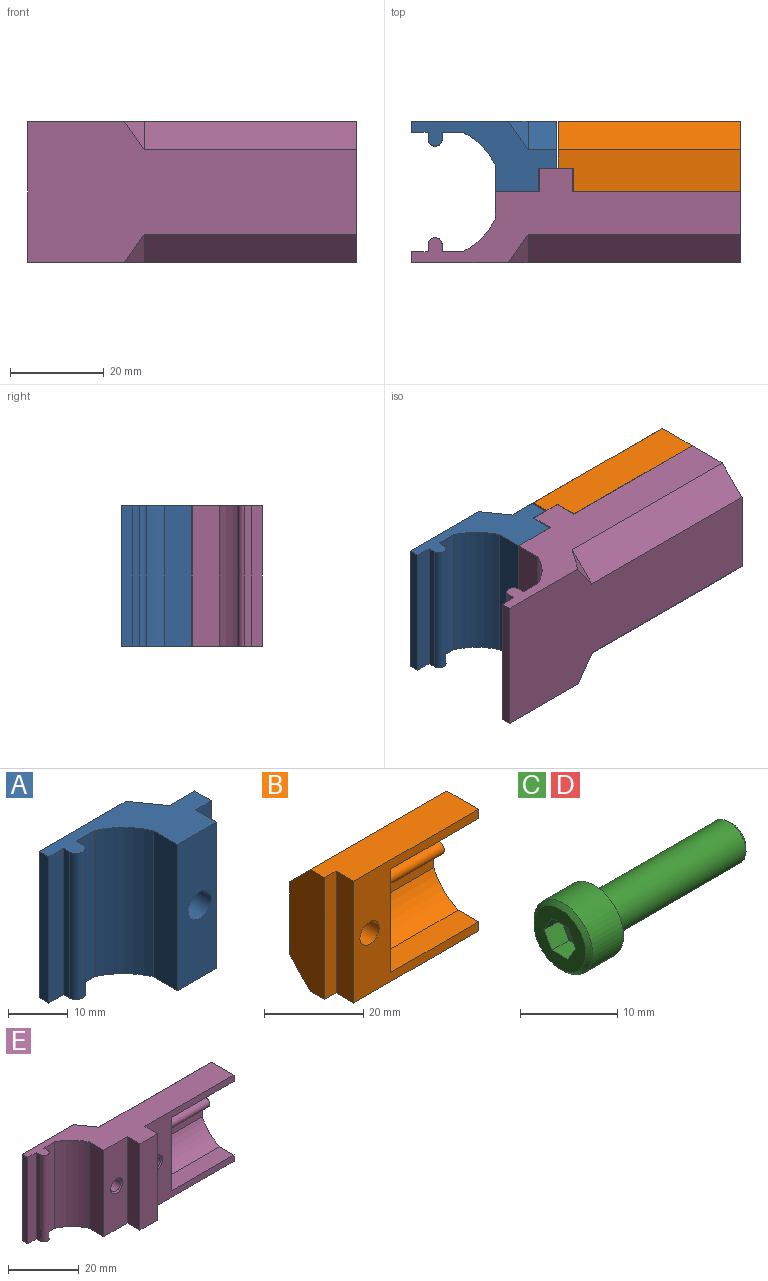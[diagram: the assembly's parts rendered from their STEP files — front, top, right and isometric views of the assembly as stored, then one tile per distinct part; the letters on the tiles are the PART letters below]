
ASSEMBLY  parts=5 mates=4
PART A: 23 faces, bbox 30.8x15x30 mm
  f0: plane 9.5x9.5mm, normal (0,1,0), area 41.7mm2, adj f1,f4
  f1: cone r=0mm half-angle=45deg, axis (0,1,0), area 7.7mm2, adj f0,f5
  f2: plane 6x6mm, normal (0,0.71,-0.71), area 50.9mm2, adj f3,f6,f8,f11
  f3: plane 6x6mm, normal (0.71,0.5,-0.5), area 25.5mm2, adj f2,f6,f11
  f4: cylinder r=4.75mm len=9.5mm, axis (0,-1,0), area 161.2mm2, adj f0,f11
  f5: cylinder r=2.75mm len=9.3mm, axis (0,-1,0), area 160.7mm2, adj f1,f20
  f6: plane 30.8x15mm, normal (0,0,-1), area 194.6mm2, adj f2,f3,f7,f8,f11,f12,f13,f14
  f7: plane 30x3.75mm, normal (0,-1,0), area 112.5mm2, adj f6,f8,f21,f22
  f8: plane 30x10mm, normal (1,0,0), area 264mm2, adj f2,f6,f7,f9,f11,f22
  f9: plane 6x6mm, normal (0,0.71,0.71), area 50.9mm2, adj f8,f10,f11,f22
  f10: plane 6x6mm, normal (0.71,0.5,0.5), area 25.5mm2, adj f9,f11,f22
  f11: plane 30.8x30mm, normal (0,1,0), area 755.7mm2, adj f2,f3,f4,f6,f8,f9,f10,f12
  f12: plane 30x2.25mm, normal (-1,0,0), area 67.5mm2, adj f6,f11,f13,f22
  f13: plane 30x3.5mm, normal (0,-1,0), area 105mm2, adj f6,f12,f14,f22
  f14: plane 30x1.5mm, normal (-1,0,0), area 45mm2, adj f6,f13,f15,f22
  f15: cylinder r=1.5mm len=30mm, axis (0,0,-1), area 141.4mm2, adj f6,f14,f16,f22
  f16: plane 30x1.5mm, normal (1,0,0), area 45mm2, adj f6,f15,f17,f22
  f17: plane 30x4.28mm, normal (0,-1,0), area 128.5mm2, adj f6,f16,f18,f22
  f18: cylinder r=14mm len=30mm, axis (0,0,-1), area 302.1mm2, adj f6,f17,f19,f22
  f19: plane 30x5.78mm, normal (-1,0,0), area 173.5mm2, adj f6,f18,f20,f22
  f20: plane 30x9.3mm, normal (0,-1,0), area 255.2mm2, adj f5,f6,f19,f21,f22
  f21: plane 30x5mm, normal (1,0,0), area 150mm2, adj f6,f7,f20,f22
  f22: plane 30.8x15mm, normal (0,0,1), area 194.6mm2, adj f7,f8,f9,f10,f11,f12,f13,f14
PART B: 24 faces, bbox 38.8x15x30 mm
  f0: plane 9.5x9.5mm, normal (0,1,0), area 41.7mm2, adj f1,f2
  f1: cone r=0mm half-angle=45deg, axis (0,1,0), area 7.7mm2, adj f0,f4
  f2: cylinder r=4.75mm len=9.5mm, axis (0,-1,0), area 161.2mm2, adj f0,f15
  f3: plane 25.5x12.75mm, normal (1,0,0), area 280.4mm2, adj f5,f6,f7,f8,f9,f10,f11,f12
  f4: cylinder r=2.75mm len=9.3mm, axis (0,-1,0), area 160.7mm2, adj f1,f19
  f5: plane 25x5.78mm, normal (0,0,-1), area 144.6mm2, adj f3,f6,f19,f20
  f6: cylinder r=14mm len=25mm, axis (1,0,0), area 251.7mm2, adj f3,f5,f7,f20
  f7: plane 25x4.28mm, normal (0,-1,0), area 107.1mm2, adj f3,f6,f8,f20
  f8: plane 25x1.5mm, normal (0,0,1), area 37.5mm2, adj f3,f7,f9,f20
  f9: cylinder r=1.5mm len=25mm, axis (1,0,0), area 117.8mm2, adj f3,f8,f10,f20
  f10: plane 25x1.5mm, normal (0,0,-1), area 37.5mm2, adj f3,f9,f11,f20
  f11: plane 25x4.28mm, normal (0,-1,0), area 107.1mm2, adj f3,f10,f12,f20
  f12: cylinder r=14mm len=25mm, axis (1,0,0), area 251.7mm2, adj f3,f11,f13,f20
  f13: plane 25x5.78mm, normal (0,0,1), area 144.6mm2, adj f3,f12,f19,f20
  f14: plane 38.8x9mm, normal (0,0,-1), area 332.9mm2, adj f16,f17,f18,f19,f20,f22
  f15: plane 38.8x18mm, normal (0,1,0), area 627.5mm2, adj f2,f16,f20,f21,f22
  f16: plane 38.8x6mm, normal (0,0.71,-0.71), area 329.2mm2, adj f14,f15,f20,f22
  f17: plane 30x3.25mm, normal (0,-1,0), area 97.5mm2, adj f14,f18,f22,f23
  f18: plane 30x5mm, normal (-1,0,0), area 150mm2, adj f14,f17,f19,f23
  f19: plane 35.55x30mm, normal (0,-1,0), area 405.2mm2, adj f3,f4,f5,f13,f14,f18,f20,f23
  f20: plane 30x15mm, normal (1,0,0), area 133.6mm2, adj f5,f6,f7,f8,f9,f10,f11,f12
  f21: plane 38.8x6mm, normal (0,0.71,0.71), area 329.2mm2, adj f15,f20,f22,f23
  f22: plane 30x10mm, normal (-1,0,0), area 264mm2, adj f14,f15,f16,f17,f21,f23
  f23: plane 38.8x9mm, normal (0,0,1), area 333mm2, adj f17,f18,f19,f20,f21,f22
PART C: 20 faces, bbox 25x8.5x8.5 mm
  f0: plane 4.02x4.02mm, normal (1,0,0), area 12.7mm2, adj f1
  f1: cone r=0mm half-angle=45deg, axis (-1,0,0), area 9.8mm2, adj f0,f2
  f2: cylinder r=2.5mm len=19.51mm, axis (1,0,0), area 306.5mm2, adj f1,f3
  f3: plane 8.5x8.5mm, normal (1,0,0), area 37.1mm2, adj f2,f5
  f4: cone r=0mm half-angle=75deg, axis (-1,0,0), area 13mm2, adj f6,f7,f8,f9,f10,f11
  f5: cylinder r=4.25mm len=8.5mm, axis (1,0,0), area 120.2mm2, adj f3,f12
  f6: plane 1.73x1mm, normal (-1,0,0), area 0.2mm2, adj f4,f13,f14
  f7: plane 1.73x1mm, normal (-1,0,0), area 0.2mm2, adj f4,f14,f15
  f8: plane 2x0.58mm, normal (-1,0,0), area 0.2mm2, adj f4,f15,f16
  f9: plane 1.73x1mm, normal (-1,0,0), area 0.2mm2, adj f4,f16,f17
  f10: plane 1.73x1mm, normal (-1,0,0), area 0.2mm2, adj f4,f17,f18
  f11: plane 2x0.58mm, normal (-1,0,0), area 0.2mm2, adj f4,f13,f18
  f12: cone r=0mm half-angle=45deg, axis (1,0,0), area 17.8mm2, adj f5,f19
  f13: plane 2.5x2mm, normal (0,0.87,0.5), area 5.8mm2, adj f6,f11,f14,f18,f19
  f14: plane 2.5x2.31mm, normal (0,0,1), area 5.8mm2, adj f6,f7,f13,f15,f19
  f15: plane 2.5x2mm, normal (0,-0.87,0.5), area 5.8mm2, adj f7,f8,f14,f16,f19
  f16: plane 2.5x2mm, normal (0,-0.87,-0.5), area 5.8mm2, adj f8,f9,f15,f17,f19
  f17: plane 2.5x2.31mm, normal (0,0,-1), area 5.8mm2, adj f9,f10,f16,f18,f19
  f18: plane 2.5x2mm, normal (0,0.87,-0.5), area 5.8mm2, adj f10,f11,f13,f17,f19
  f19: plane 7.5x7.5mm, normal (-1,0,0), area 30.3mm2, adj f12,f13,f14,f15,f16,f17,f18
PART D: same geometry as C
PART E: 37 faces, bbox 70x20x30 mm
  f0: cone r=0mm half-angle=60deg, axis (0,-1,0), area 15.5mm2, adj f1
  f1: cylinder r=2.07mm len=10.17mm, axis (0,-1,0), area 132mm2, adj f0,f12
  f2: cylinder r=14mm len=25mm, axis (1,0,0), area 251.7mm2, adj f3,f10,f11,f17
  f3: plane 25x4.28mm, normal (0,-1,0), area 107.1mm2, adj f2,f4,f10,f17
  f4: plane 25x1.5mm, normal (0,0,1), area 37.5mm2, adj f3,f5,f10,f17
  f5: cylinder r=1.5mm len=25mm, axis (1,0,0), area 117.8mm2, adj f4,f6,f10,f17
  f6: plane 25x1.5mm, normal (0,0,-1), area 37.5mm2, adj f5,f7,f10,f17
  f7: plane 25x4.28mm, normal (0,-1,0), area 107.1mm2, adj f6,f8,f10,f17
  f8: cylinder r=14mm len=25mm, axis (1,0,0), area 251.7mm2, adj f7,f9,f10,f17
  f9: plane 25x5.78mm, normal (0,0,1), area 144.6mm2, adj f8,f10,f17,f18
  f10: plane 25.5x12.75mm, normal (1,0,0), area 280.4mm2, adj f2,f3,f4,f5,f6,f7,f8,f9
  f11: plane 25x5.78mm, normal (0,0,-1), area 144.6mm2, adj f2,f10,f17,f18
  f12: cone r=0mm half-angle=45deg, axis (0,-1,0), area 8.8mm2, adj f1,f18
  f13: cone r=0mm half-angle=60deg, axis (0,-1,0), area 15.5mm2, adj f30
  f14: plane 45.2x6mm, normal (0,0.71,0.71), area 383.5mm2, adj f15,f17,f28,f32
  f15: plane 6x6mm, normal (0.71,0.5,0.5), area 25.5mm2, adj f14,f28,f32
  f16: plane 45.2x6mm, normal (0,0.71,-0.71), area 383.5mm2, adj f17,f28,f29,f34
  f17: plane 30x15mm, normal (1,0,0), area 133.6mm2, adj f2,f3,f4,f5,f6,f7,f8,f9
  f18: plane 35.7x30mm, normal (0,-1,0), area 413.9mm2, adj f9,f10,f11,f12,f17,f19,f32,f34
  f19: plane 30x5mm, normal (1,0,0), area 150mm2, adj f18,f20,f32,f34
  f20: plane 30x7mm, normal (0,-1,0), area 210mm2, adj f19,f31,f32,f34
  f21: cylinder r=14mm len=30mm, axis (0,0,-1), area 302.1mm2, adj f22,f32,f33,f34
  f22: plane 30x4.28mm, normal (0,-1,0), area 128.5mm2, adj f21,f23,f32,f34
  f23: plane 30x1.5mm, normal (1,0,0), area 45mm2, adj f22,f24,f32,f34
  f24: cylinder r=1.5mm len=30mm, axis (0,0,-1), area 141.4mm2, adj f23,f25,f32,f34
  f25: plane 30x1.5mm, normal (-1,0,0), area 45mm2, adj f24,f26,f32,f34
  f26: plane 30x3.5mm, normal (0,-1,0), area 105mm2, adj f25,f27,f32,f34
  f27: plane 30x2.25mm, normal (-1,0,0), area 67.5mm2, adj f26,f28,f32,f34
  f28: plane 70x30mm, normal (0,1,0), area 1532.1mm2, adj f14,f15,f16,f17,f27,f29,f32,f34
  f29: plane 6x6mm, normal (0.71,0.5,-0.5), area 25.5mm2, adj f16,f28,f34
  f30: cylinder r=2.07mm len=10.17mm, axis (0,-1,0), area 132mm2, adj f13,f35
  f31: plane 30x5mm, normal (-1,0,0), area 150mm2, adj f20,f32,f34,f36
  f32: plane 70x20mm, normal (0,0,1), area 601.1mm2, adj f14,f15,f17,f18,f19,f20,f21,f22
  f33: plane 30x5.78mm, normal (-1,0,0), area 173.5mm2, adj f21,f32,f34,f36
  f34: plane 70x20mm, normal (0,0,-1), area 601.1mm2, adj f16,f17,f18,f19,f20,f21,f22,f23
  f35: cone r=0mm half-angle=45deg, axis (0,-1,0), area 8.8mm2, adj f30,f36
  f36: plane 30x9.55mm, normal (0,-1,0), area 266.9mm2, adj f31,f32,f33,f34,f35
PLACE A t=(-7.14,-22.58,-11.41)mm
PLACE B t=(24.06,-22.58,-11.41)mm
PLACE C rot(axis=(0.58,-0.58,-0.58),120deg) t=(15.86,-12.98,-11.41)mm
PLACE D rot(axis=(0.58,-0.58,-0.58),120deg) t=(31.86,-12.98,-11.41)mm
PLACE E rot(axis=(1,0,0),180deg) t=(-7.14,-22.58,-11.41)mm
MATE fastened C.f1 <-> A.f1  axis (0,-1,0) through (15.86,-12.98,-11.41)mm
MATE fastened D.f1 <-> B.f1  axis (0,-1,0) through (31.86,-12.98,-11.41)mm
MATE fastened A.f1 <-> E.f13  axis (0,-1,0) through (15.86,-22.58,-11.41)mm
MATE fastened B.f1 <-> E.f0  axis (0,-1,0) through (31.86,-22.58,-11.41)mm
